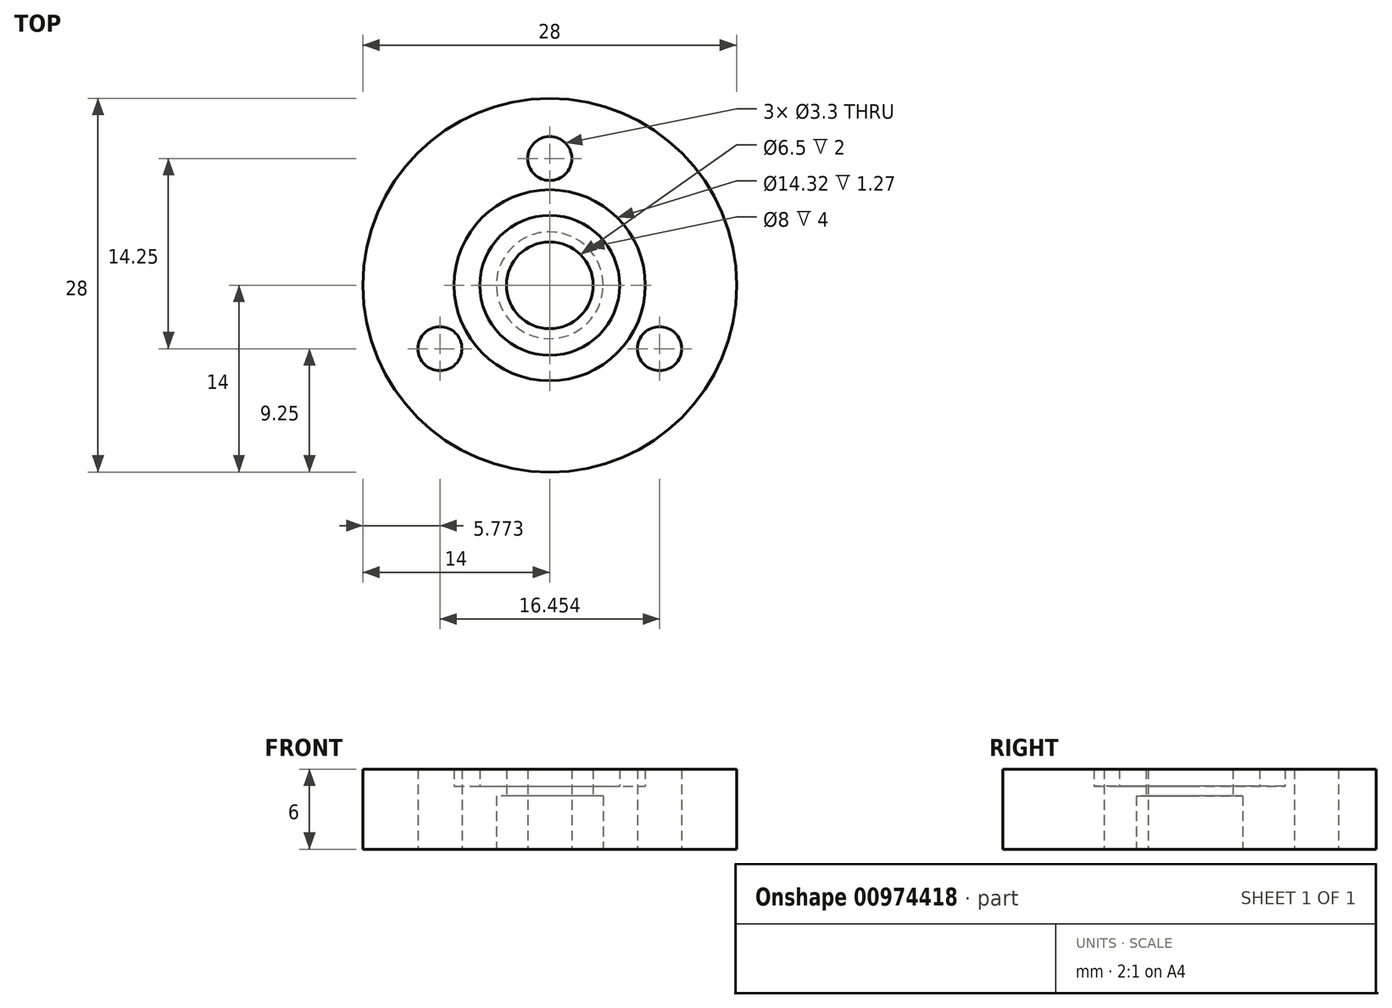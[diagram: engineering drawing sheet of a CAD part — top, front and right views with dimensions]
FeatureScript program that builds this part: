
annotation { "Feature Type Name" : "Feature", "Feature Type Description" : "" }
export const myFeature = defineFeature(function(context is Context, id is Id, definition is map)
    precondition{}
    {
        {
            var Q0;
            Q0=qCreatedBy(makeId("Top.planeOp"),FACE);
            var sketch = newSketch(context, id + "F0", { "sketchPlane" : qUnion([Q0])});
            skCircle(sketch, "E0", {"center": v(0, 0) * mm, "radius": 14 * mm});
            skCircle(sketch, "E1", {"center": v(0, 9.5) * mm, "radius": 1.65 * mm});
            skCircle(sketch, "E2.1.0", {"center": v(-8.23, -4.75) * mm, "radius": 1.65 * mm});
            skCircle(sketch, "E2.2.0", {"center": v(8.23, -4.75) * mm, "radius": 1.65 * mm});
            skCircle(sketch, "E3", {"center": v(0, 0) * mm, "radius": 4 * mm});
            skCircle(sketch, "E4", {"center": v(0, 0) * mm, "radius": 3.25 * mm});
            skSolve(sketch);
        }
        {
            var Q0;
            Q0=makeQuery(id+"F0.imprint","IMPRINT",FACE,{"disambiguationData":[TD([[makeQuery(id+"F0.imprint","IMPRINT",EDGE,{"derivedFrom":sQuery(id+"F0.wireOp",EDGE,"E0")}),1.0]])]});
            var Q1;
            Q1=makeQuery(id+"F0.imprint","IMPRINT",FACE,{"disambiguationData":[TD([[makeQuery(id+"F0.imprint","IMPRINT",EDGE,{"derivedFrom":sQuery(id+"F0.wireOp",EDGE,"E3")}),1.0]])]});
            extrude(context, id + "F1", {"entities" : qUnion([Q0, Q1]), "depth" : 6 * mm, "offsetDistance" : 25 * mm});
        }
        {
            var Q0;
            Q0=qCreatedBy(makeId("Right.planeOp"),FACE);
            var sketch = newSketch(context, id + "F2", { "sketchPlane" : qUnion([Q0])});
            skLineSegment(sketch, "E5.bottom", {"start": v(5.24, 6) * mm, "end": v(7.16, 6) * mm});
            skLineSegment(sketch, "E5.top", {"start": v(5.24, 4.73) * mm, "end": v(7.16, 4.73) * mm});
            skLineSegment(sketch, "E5.left", {"start": v(5.24, 6) * mm, "end": v(5.24, 4.73) * mm});
            skLineSegment(sketch, "E5.right", {"start": v(7.16, 6) * mm, "end": v(7.16, 4.73) * mm});
            skLineSegment(sketch, "E6", {"start": v(0, 7.22) * mm, "end": v(0, -3.43) * mm, "construction": true});
            skSolve(sketch);
        }
        {
            var Q0;
            Q0=makeQuery(id+"F2.imprint","IMPRINT",FACE,{"disambiguationData":[TD([[makeQuery(id+"F2.imprint","IMPRINT",EDGE,{"derivedFrom":sQuery(id+"F2.wireOp",EDGE,"E5.bottom")}),-1.0]])]});
            var Q1;
            Q1=sQuery(id+"F2.wireOp",EDGE,"E6");
            revolve(context, id + "F3", {"operationType" : NewBodyOperationType.REMOVE, "surfaceOperationType" : NewSurfaceOperationType.NEW, "entities" : qUnion([Q0]), "axis" : qUnion([Q1]), "revolveType" : RevolveType.FULL, "oppositeDirection" : true});
        }
        {
            var Q0;
            Q0=makeQuery(id+"F0.imprint","IMPRINT",FACE,{"disambiguationData":[TD([[makeQuery(id+"F0.imprint","IMPRINT",EDGE,{"derivedFrom":sQuery(id+"F0.wireOp",EDGE,"E3")}),1.0]])]});
            extrude(context, id + "F4", {"entities" : qUnion([Q0]), "operationType" : NewBodyOperationType.REMOVE, "depth" : 4 * mm, "offsetDistance" : 25 * mm});
        }
    });
